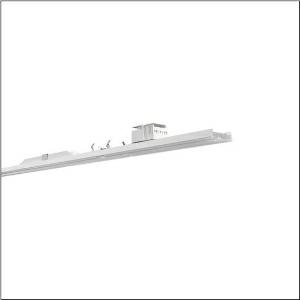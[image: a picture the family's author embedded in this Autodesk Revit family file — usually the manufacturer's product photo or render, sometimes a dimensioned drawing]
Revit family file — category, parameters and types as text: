
# Revit family: licross_r__21_recessed_mo_52tl14dne7xf_5002
name_source: partatom
category: Lighting Fixtures
units: mm (PartAtom-declared; Revit-internal decimal feet)

## family parameters
Cut with Voids When Loaded = No
Host = Face
Light Source = No
Part Type = Normal
Room Calculation Point = No
Round Connector Dimension = Use Diameter
Shared = No

## types (1)
- --- (1 x LED, 7340 lm, 61.1 W, 5000K)
    Apparent Load = 61 VA
    CIE Flux Codes = 56 84 97 100 100
    Color Rendering = 90
    Color Temperature = 5000K
    Default Elevation = 1800 mm
    Description = Licross® 21 Recessed MO, luminaire insert, of sheet steel, galvanised, coil coated, white, length: 1.500mm, width: 66mm, height: 67mm, LED rated luminous flux: 7.340lm, light colour: 950, control gear: DALI 2, control gear: ECG DALI, with plug, 5-pole, with phase selection, mains connection: 220..240V, AC, 50/60Hz, halogen-free wiring, primary optical cover: cover, of PMMA, light emission: direct distribution, primary light characteristic: asymmetric, protection rating (complete): IP40, insulation class (complete): insulation class I (protective earthing), certification: CE, ENEC, VDE, UKCA, protection symbol: D if used in an environment without relevant dust loads with corresponding accessories, permissible ambient temperature for indoor applications: -25..+35°C, corresponds to IFS (International Featured Standards) requirements for safety and quality in the food industry, reducing of maximum allowable ambient temperature of 5°C with ceiling mounting, packaging unit: 1 piece
    Height = 58 mm
    Lamp = 1 x LED
    Lamp Light Flux = 7340 lm
    Lamp Power = 61.1 W
    Lamp count = 1
    Length = 1500 mm
    Luminous efficacy = 120 lm/W
    Manufacturer = Siteco
    ModVariant = No
    Model = 52TL14DNE7XF
    Mounting Place = Ceiling
    Mounting Type = Pendant
    Number of Poles = 1
    OnlyDefault = Yes
    Power Factor = 1
    Product Name = Licross® 21 Recessed MO
    Product group = luminaire insert
    ProductGroupID = 902
    Protection Class = Protection class I
    Protection Degree = IP 40
    RLX_Detail_Level = 1
    RlxData = <blob elided: 22909 chars, md5=98b9dcb2>
    Socket = socket
    Standby Power = 0 W
    System Light Flux = 7340 lm
    System Power = 61 W
    Type Comments = factory setting: luminous flux: 100 % | dim-lin: 254 | 405 mA
    Type Image = l_1266722.jpg
    URL = http://relux.com
    VarID = @adj_129197
    Voltage = 0 V
    Weight = 0.00 kg
    Width = 66 mm

## geometry (parser evidence)
native form markers: Blend x4, Sweep x10
no freeform markers — native parametric forms only
